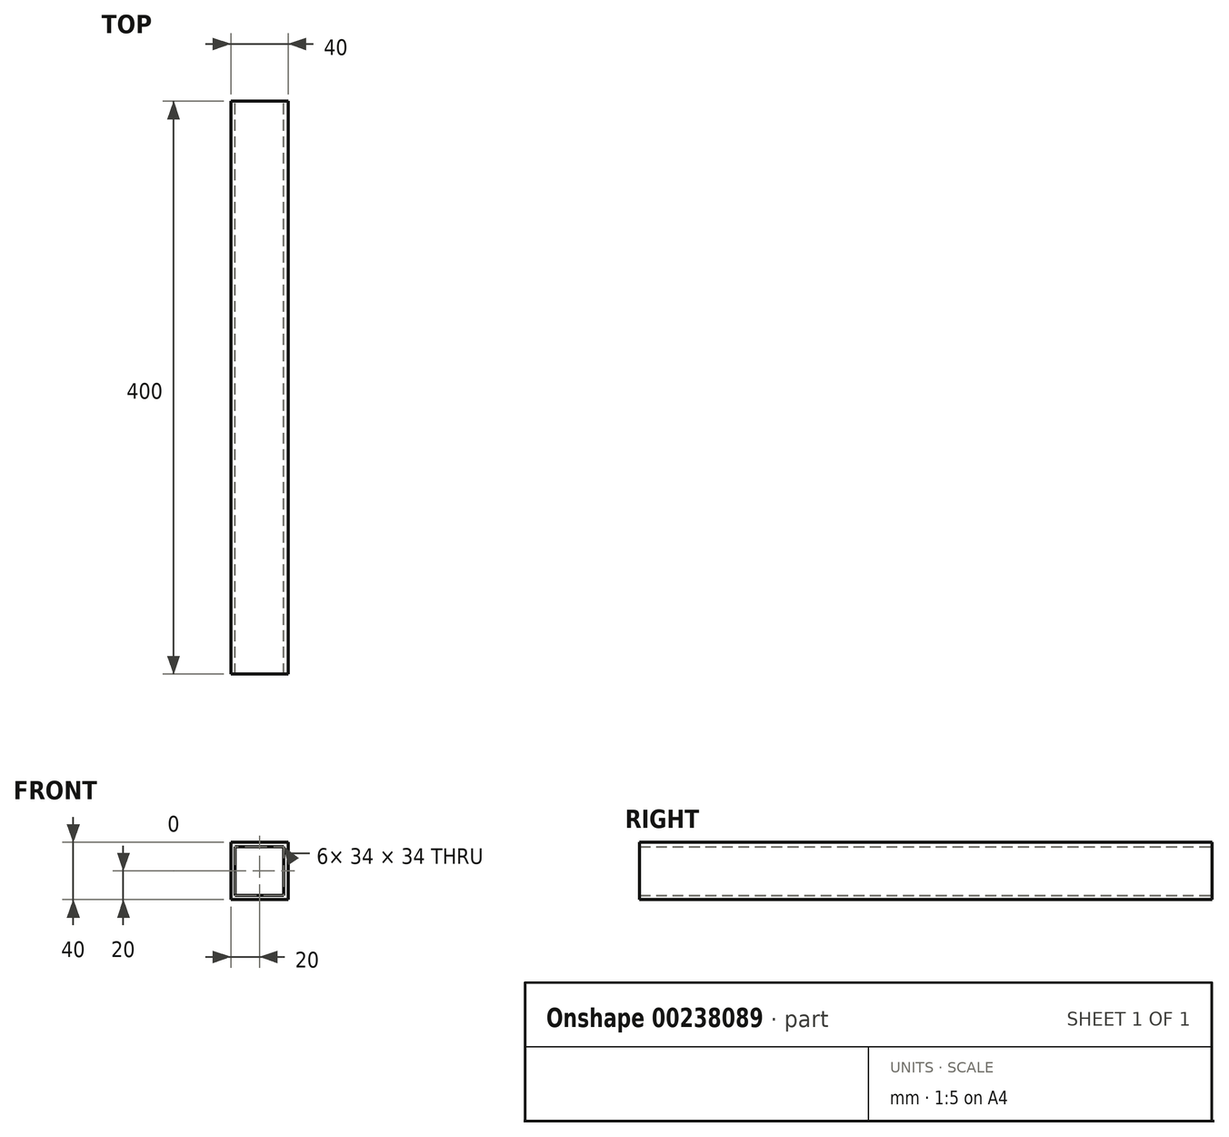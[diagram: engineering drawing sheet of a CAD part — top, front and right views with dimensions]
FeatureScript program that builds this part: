
annotation { "Feature Type Name" : "Feature", "Feature Type Description" : "" }
export const myFeature = defineFeature(function(context is Context, id is Id, definition is map)
    precondition{}
    {
        {
            var Q0;
            Q0=qCreatedBy(makeId("Front.planeOp"),FACE);
            var sketch = newSketch(context, id + "F0", { "sketchPlane" : qUnion([Q0])});
            skLineSegment(sketch, "E0.bottom", {"start": v(-20, 20) * mm, "end": v(20, 20) * mm});
            skLineSegment(sketch, "E0.top", {"start": v(-20, -20) * mm, "end": v(20, -20) * mm});
            skLineSegment(sketch, "E0.left", {"start": v(-20, 20) * mm, "end": v(-20, -20) * mm});
            skLineSegment(sketch, "E0.right", {"start": v(20, 20) * mm, "end": v(20, -20) * mm});
            skPoint(sketch, "E0.middle", {"position": v(0, 0) * mm});
            skLineSegment(sketch, "E1.bottom", {"start": v(17, 17) * mm, "end": v(-17, 17) * mm});
            skLineSegment(sketch, "E1.top", {"start": v(17, -17) * mm, "end": v(-17, -17) * mm});
            skLineSegment(sketch, "E1.left", {"start": v(17, 17) * mm, "end": v(17, -17) * mm});
            skLineSegment(sketch, "E1.right", {"start": v(-17, 17) * mm, "end": v(-17, -17) * mm});
            skSolve(sketch);
        }
        {
            var Q0;
            Q0=makeQuery(id+"F0.imprint","IMPRINT",FACE,{"disambiguationData":[TD([[makeQuery(id+"F0.imprint","IMPRINT",EDGE,{"derivedFrom":sQuery(id+"F0.wireOp",EDGE,"E0.bottom")}),-1.0]])]});
            extrude(context, id + "F1", {"entities" : qUnion([Q0]), "depth" : 400 * mm});
        }
    });
